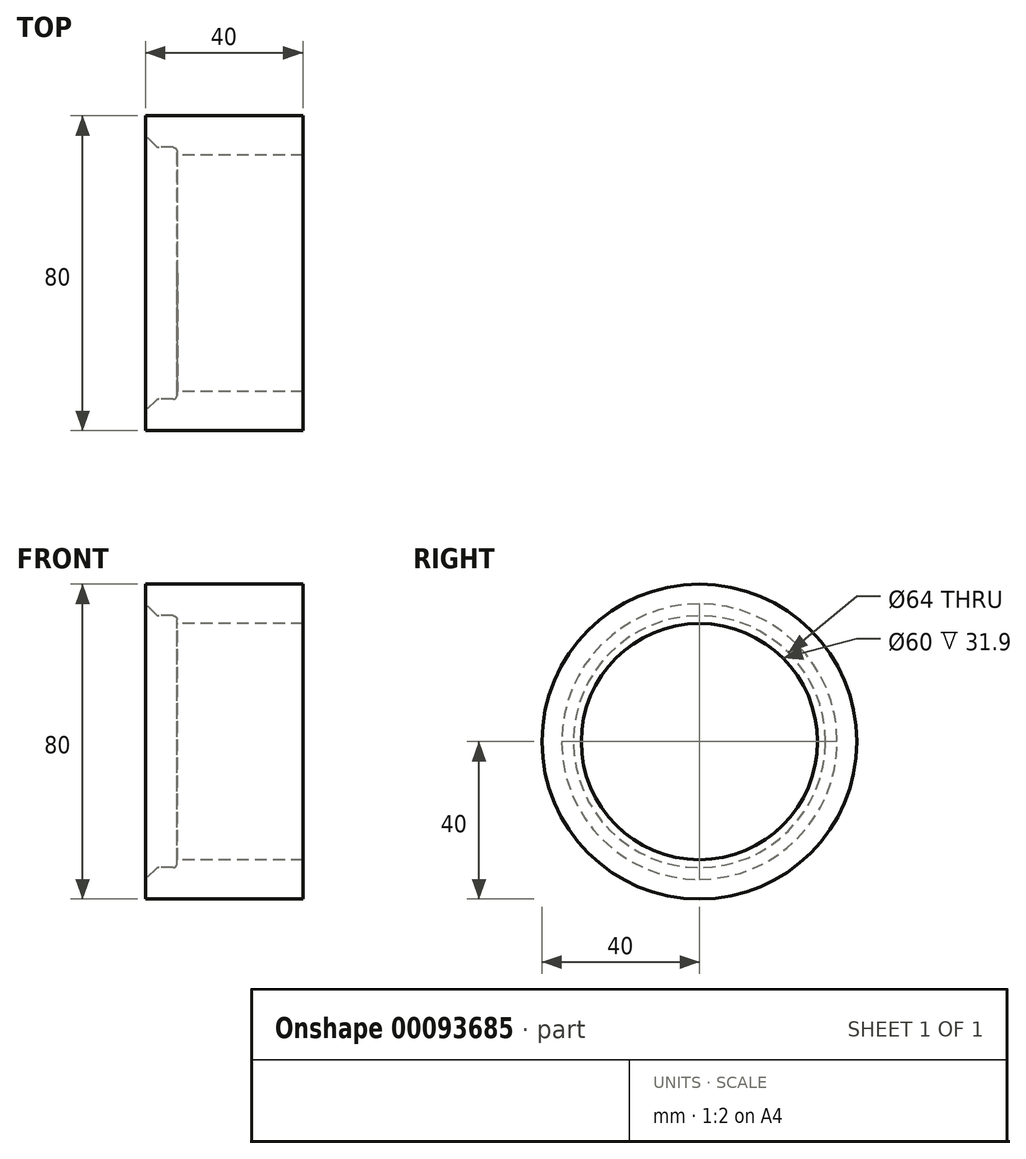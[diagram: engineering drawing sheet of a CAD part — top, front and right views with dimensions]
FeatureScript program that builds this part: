
annotation { "Feature Type Name" : "Feature", "Feature Type Description" : "" }
export const myFeature = defineFeature(function(context is Context, id is Id, definition is map)
    precondition{}
    {
        {
            var Q0;
            Q0=qCreatedBy(makeId("Top.planeOp"),FACE);
            var sketch = newSketch(context, id + "F0", { "sketchPlane" : qUnion([Q0])});
            skLineSegment(sketch, "E0", {"start": v(0, 40) * mm, "end": v(0, 32) * mm});
            skLineSegment(sketch, "E1", {"start": v(0, 32) * mm, "end": v(8, 32) * mm});
            skLineSegment(sketch, "E2", {"start": v(8, 32) * mm, "end": v(8, 30) * mm});
            skLineSegment(sketch, "E3", {"start": v(8, 30) * mm, "end": v(40, 30) * mm});
            skLineSegment(sketch, "E4", {"start": v(40, 30) * mm, "end": v(40, 40) * mm});
            skLineSegment(sketch, "E5", {"start": v(40, 40) * mm, "end": v(0, 40) * mm});
            skLineSegment(sketch, "E6", {"start": v(-179.88, 0) * mm, "end": v(174.93, 0) * mm, "construction": true});
            skSolve(sketch);
        }
        {
            var Q0;
            Q0 = qSketchRegion(id + "F0", true);
            var Q1;
            Q1=sQuery(id+"F0.wireOp",EDGE,"E6");
            revolve(context, id + "F1", {"entities" : qUnion([Q0]), "axis" : qUnion([Q1]), "revolveType" : RevolveType.FULL});
        }
        {
            var Q0;
            Q0=makeQuery(id+"F1.opRevolve","SWEPT_EDGE",EDGE,{"disambiguationData":[OSD([sQuery(id+"F0.wireOp",EDGE,"E0"),sQuery(id+"F0.wireOp",EDGE,"E1")])]});
            chamfer(context, id + "F2", {"entities" : qUnion([Q0]), "width" : 3 * mm, "tangentPropagation" : true});
        }
        {
            var Q0;
            Q0=makeQuery(id+"F1.opRevolve","SWEPT_EDGE",EDGE,{"disambiguationData":[OSD([sQuery(id+"F0.wireOp",EDGE,"E1"),sQuery(id+"F0.wireOp",EDGE,"E2")])]});
            var Q1;
            {var subQ0=sQuery(id+"F0.wireOp",EDGE,"E1");Q1=makeQuery(id+"F2.opChamfer","BLEND_EDGE",EDGE,{"blendedFrom":[makeQuery(id+"F1.opRevolve","SWEPT_EDGE",EDGE,{"disambiguationData":[OSD([sQuery(id+"F0.wireOp",EDGE,"E0"),subQ0])]}),makeQuery(id+"F1.opRevolve","SWEPT_FACE",FACE,{"disambiguationData":[OSD([subQ0])]})],"blendedInto":[makeQuery(id+"F1.opRevolve","SWEPT_FACE",FACE,{"disambiguationData":[OSD([subQ0])]})]});}
            fillet(context, id + "F3", {"entities" : qUnion([Q0, Q1]), "radius" : 1 * mm, "tangentPropagation" : true, "allowEdgeOverflow" : false});
        }
        {
            var Q0;
            Q0=makeQuery(id+"F1.opRevolve","SWEPT_EDGE",EDGE,{"disambiguationData":[OSD([sQuery(id+"F0.wireOp",EDGE,"E2"),sQuery(id+"F0.wireOp",EDGE,"E3")])]});
            chamfer(context, id + "F4", {"entities" : qUnion([Q0]), "width" : 0.1 * mm, "tangentPropagation" : true});
        }
    });
